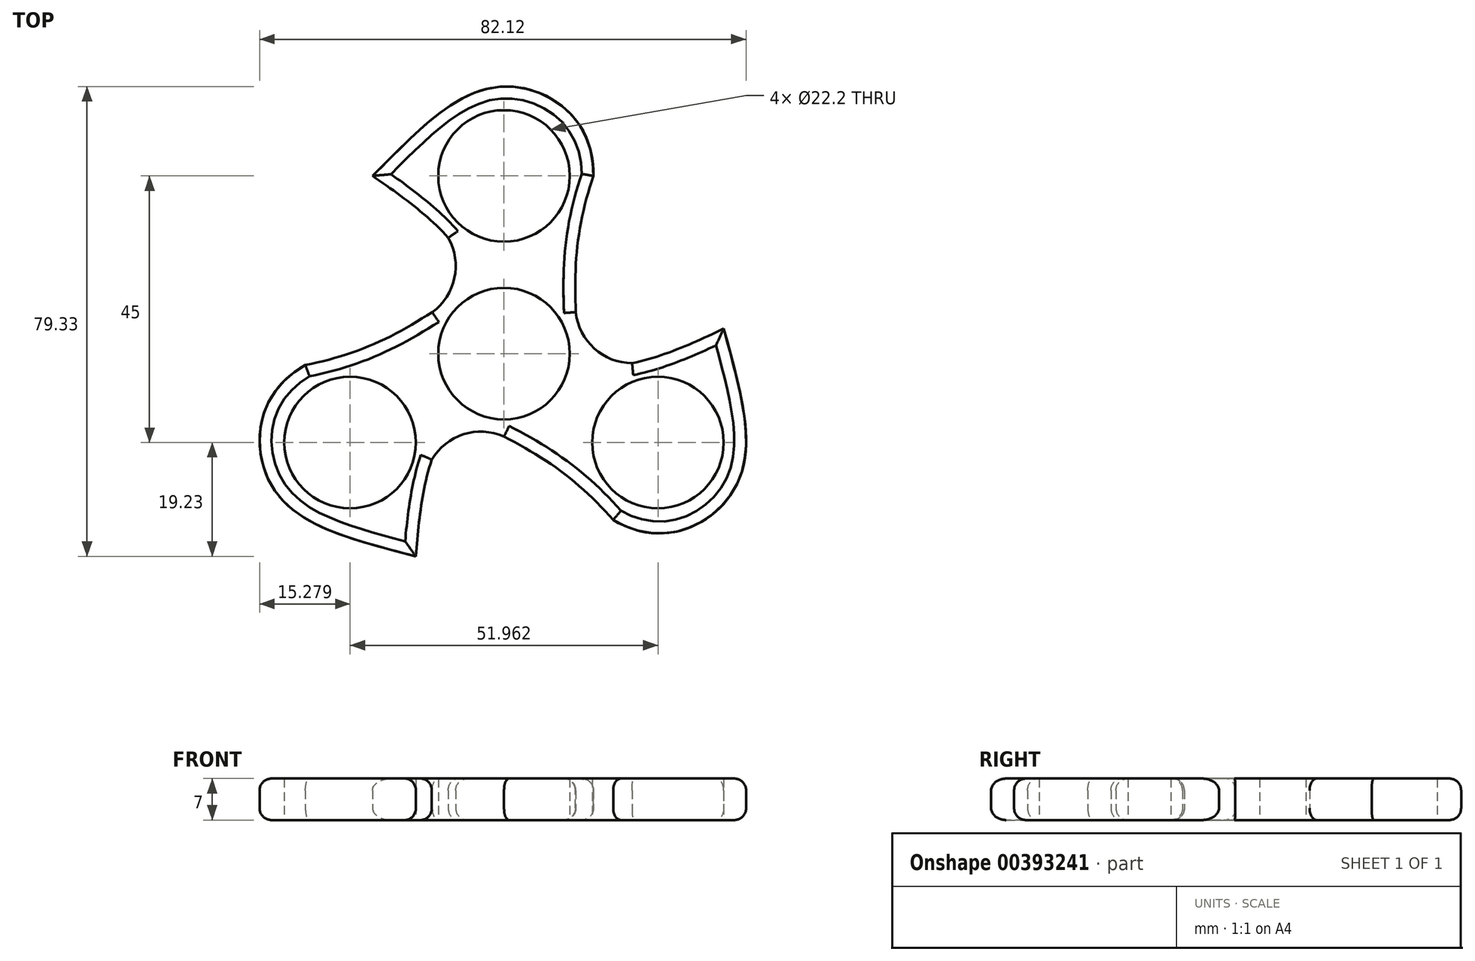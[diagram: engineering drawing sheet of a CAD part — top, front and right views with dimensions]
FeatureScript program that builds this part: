
annotation { "Feature Type Name" : "Feature", "Feature Type Description" : "" }
export const myFeature = defineFeature(function(context is Context, id is Id, definition is map)
    precondition{}
    {
        {
            var Q0;
            Q0=qCreatedBy(makeId("Top.planeOp"),FACE);
            var sketch = newSketch(context, id + "F0", { "sketchPlane" : qUnion([Q0])});
            skCircle(sketch, "E0", {"center": v(0, 0) * mm, "radius": 11.1 * mm});
            skCircle(sketch, "E1", {"center": v(0, 30) * mm, "radius": 11.1 * mm});
            skLineSegment(sketch, "E2", {"start": v(0, 0) * mm, "end": v(0, 30) * mm, "construction": true});
            skLineSegment(sketch, "E3", {"start": v(0, 30) * mm, "end": v(-22.2, 30) * mm, "construction": true});
            skLineSegment(sketch, "E4", {"start": v(0, 30) * mm, "end": v(15.1, 30) * mm, "construction": true});
            skLineSegment(sketch, "E5", {"start": v(0, 30) * mm, "end": v(0, 45.1) * mm, "construction": true});
            skLineSegment(sketch, "E6.1.0", {"start": v(-25.98, -15) * mm, "end": v(-33.53, -1.92) * mm, "construction": true});
            skLineSegment(sketch, "E6.1.1", {"start": v(-25.98, -15) * mm, "end": v(-39.06, -22.55) * mm, "construction": true});
            skLineSegment(sketch, "E6.1.2", {"start": v(-25.98, -15) * mm, "end": v(-14.88, -34.23) * mm, "construction": true});
            skCircle(sketch, "E6.1.3", {"center": v(-25.98, -15) * mm, "radius": 11.1 * mm});
            skLineSegment(sketch, "E6.1.4", {"start": v(0, 0) * mm, "end": v(-25.98, -15) * mm, "construction": true});
            skLineSegment(sketch, "E6.2.0", {"start": v(25.98, -15) * mm, "end": v(18.43, -28.08) * mm, "construction": true});
            skLineSegment(sketch, "E6.2.1", {"start": v(25.98, -15) * mm, "end": v(39.06, -22.55) * mm, "construction": true});
            skLineSegment(sketch, "E6.2.2", {"start": v(25.98, -15) * mm, "end": v(37.08, 4.23) * mm, "construction": true});
            skCircle(sketch, "E6.2.3", {"center": v(25.98, -15) * mm, "radius": 11.1 * mm});
            skLineSegment(sketch, "E6.2.4", {"start": v(0, 0) * mm, "end": v(25.98, -15) * mm, "construction": true});
            skLineSegment(sketch, "E7", {"start": v(0, 0) * mm, "end": v(-12.12, 7) * mm, "construction": true});
            skLineSegment(sketch, "E8.1.0", {"start": v(0, 0) * mm, "end": v(0, -14) * mm, "construction": true});
            skLineSegment(sketch, "E8.2.0", {"start": v(0, 0) * mm, "end": v(12.12, 7) * mm, "construction": true});
            skFitSpline(sketch, "E9", {"points": [v(-22.2, 30) * mm, v(0, 45.1) * mm, v(15.1, 30) * mm], "startDerivative": vector(44.63, 44.58) * mm, "endDerivative": vector(-1.2, -64.1) * mm});
            skFitSpline(sketch, "E10", {"points": [v(37.08, 4.23) * mm, v(39.06, -22.55) * mm, v(18.43, -28.08) * mm], "startDerivative": vector(16.3, -60.94) * mm, "endDerivative": vector(-54.91, 33.08) * mm});
            skFitSpline(sketch, "E11", {"points": [v(-14.88, -34.23) * mm, v(-39.06, -22.55) * mm, v(-33.53, -1.92) * mm], "startDerivative": vector(-60.93, 16.36) * mm, "endDerivative": vector(56.1, 31.02) * mm});
            skFitSpline(sketch, "E12", {"points": [v(15.1, 30) * mm, v(12.12, 7) * mm, v(37.08, 4.23) * mm], "startDerivative": vector(-19.55, -57.1) * mm, "endDerivative": vector(141.73, 68.98) * mm});
            skFitSpline(sketch, "E13", {"points": [v(18.43, -28.08) * mm, v(0, -14) * mm, v(-14.88, -34.23) * mm], "startDerivative": vector(-39.67, 45.48) * mm, "endDerivative": vector(-11.12, -157.23) * mm});
            skFitSpline(sketch, "E14", {"points": [v(-33.53, -1.92) * mm, v(-12.12, 7) * mm, v(-22.2, 30) * mm], "startDerivative": vector(59.23, 11.62) * mm, "endDerivative": vector(-130.6, 88.25) * mm});
            skLineSegment(sketch, "E15", {"start": v(18.43, -28.08) * mm, "end": v(27.06, -33.28) * mm});
            skLineSegment(sketch, "E16.1.0", {"start": v(15.1, 30) * mm, "end": v(15.29, 40.07) * mm});
            skLineSegment(sketch, "E16.2.0", {"start": v(-33.53, -1.92) * mm, "end": v(-42.35, -6.8) * mm});
            skArc(sketch, "E17", {"start": v(-12.12, 7) * mm, "mid": v(-8.38, 12.75) * mm, "end": v(-9.42, 19.53) * mm});
            skArc(sketch, "E18.1.0", {"start": v(0, -14) * mm, "mid": v(-6.85, -13.63) * mm, "end": v(-12.2, -17.92) * mm});
            skArc(sketch, "E18.2.0", {"start": v(12.12, 7) * mm, "mid": v(15.23, 0.88) * mm, "end": v(21.62, -1.61) * mm});
            skSolve(sketch);
        }
        {
            var Q0;
            Q0=makeQuery(id+"F0.imprint","IMPRINT",FACE,{"disambiguationData":[TD([[makeQuery(id+"F0.imprint","IMPRINT",EDGE,{"derivedFrom":sQuery(id+"F0.wireOp",EDGE,"E0")}),-1.0]])]});
            var Q1;
            {var subQ0=sQuery(id+"F0.wireOp",EDGE,"E17");Q1=makeQuery(id+"F0.imprint","IMPRINT",FACE,{"disambiguationData":[TD([[makeQuery(id+"F0.imprint","IMPRINT",EDGE,{"derivedFrom":subQ0}),-1.0]])]});}
            var Q2;
            {var subQ0=sQuery(id+"F0.wireOp",EDGE,"E18.1.0");Q2=makeQuery(id+"F0.imprint","IMPRINT",FACE,{"disambiguationData":[TD([[makeQuery(id+"F0.imprint","IMPRINT",EDGE,{"derivedFrom":subQ0}),-1.0]])]});}
            var Q3;
            {var subQ0=sQuery(id+"F0.wireOp",EDGE,"E18.2.0");Q3=makeQuery(id+"F0.imprint","IMPRINT",FACE,{"disambiguationData":[TD([[makeQuery(id+"F0.imprint","IMPRINT",EDGE,{"derivedFrom":subQ0}),-1.0]])]});}
            extrude(context, id + "F1", {"entities" : qUnion([Q0, Q1, Q2, Q3]), "endBound" : BoundingType.SYMMETRIC, "depth" : 7 * mm, "offsetDistance" : 25 * mm});
        }
        {
            var Q0;
            Q0=makeQuery(id+"F1.opExtrude","CAP_EDGE",EDGE,{"disambiguationData":[OSD([sQuery(id+"F0.wireOp",EDGE,"E9")])],"isStart":false});
            var Q1;
            Q1=makeQuery(id+"F1.opExtrude","CAP_EDGE",EDGE,{"disambiguationData":[OSD([sQuery(id+"F0.wireOp",EDGE,"E12")])],"isStart":false});
            var Q2;
            Q2=makeQuery(id+"F1.opExtrude","CAP_EDGE",EDGE,{"disambiguationData":[OSD([sQuery(id+"F0.wireOp",EDGE,"E10")])],"isStart":false});
            var Q3;
            Q3=makeQuery(id+"F1.opExtrude","CAP_EDGE",EDGE,{"disambiguationData":[OSD([sQuery(id+"F0.wireOp",EDGE,"E13")])],"isStart":false});
            var Q4;
            Q4=makeQuery(id+"F1.opExtrude","CAP_EDGE",EDGE,{"disambiguationData":[OSD([sQuery(id+"F0.wireOp",EDGE,"E11")])],"isStart":false});
            var Q5;
            Q5=makeQuery(id+"F1.opExtrude","CAP_EDGE",EDGE,{"disambiguationData":[OSD([sQuery(id+"F0.wireOp",EDGE,"E14")])],"isStart":false});
            fillet(context, id + "F2", {"entities" : qUnion([Q0, Q1, Q2, Q3, Q4, Q5]), "radius" : 2 * mm, "tangentPropagation" : true, "allowEdgeOverflow" : false});
        }
        {
            var Q0;
            Q0=makeQuery(id+"F1.opExtrude","CAP_EDGE",EDGE,{"disambiguationData":[OSD([sQuery(id+"F0.wireOp",EDGE,"E10")])],"isStart":true});
            var Q1;
            Q1=makeQuery(id+"F1.opExtrude","CAP_EDGE",EDGE,{"disambiguationData":[OSD([sQuery(id+"F0.wireOp",EDGE,"E12")])],"isStart":true});
            var Q2;
            Q2=makeQuery(id+"F1.opExtrude","CAP_EDGE",EDGE,{"disambiguationData":[OSD([sQuery(id+"F0.wireOp",EDGE,"E13")])],"isStart":true});
            var Q3;
            Q3=makeQuery(id+"F1.opExtrude","CAP_EDGE",EDGE,{"disambiguationData":[OSD([sQuery(id+"F0.wireOp",EDGE,"E11")])],"isStart":true});
            var Q4;
            Q4=makeQuery(id+"F1.opExtrude","CAP_EDGE",EDGE,{"disambiguationData":[OSD([sQuery(id+"F0.wireOp",EDGE,"E14")])],"isStart":true});
            var Q5;
            Q5=makeQuery(id+"F1.opExtrude","CAP_EDGE",EDGE,{"disambiguationData":[OSD([sQuery(id+"F0.wireOp",EDGE,"E9")])],"isStart":true});
            fillet(context, id + "F3", {"entities" : qUnion([Q0, Q1, Q2, Q3, Q4, Q5]), "radius" : 2 * mm, "tangentPropagation" : true, "allowEdgeOverflow" : false});
        }
    });
